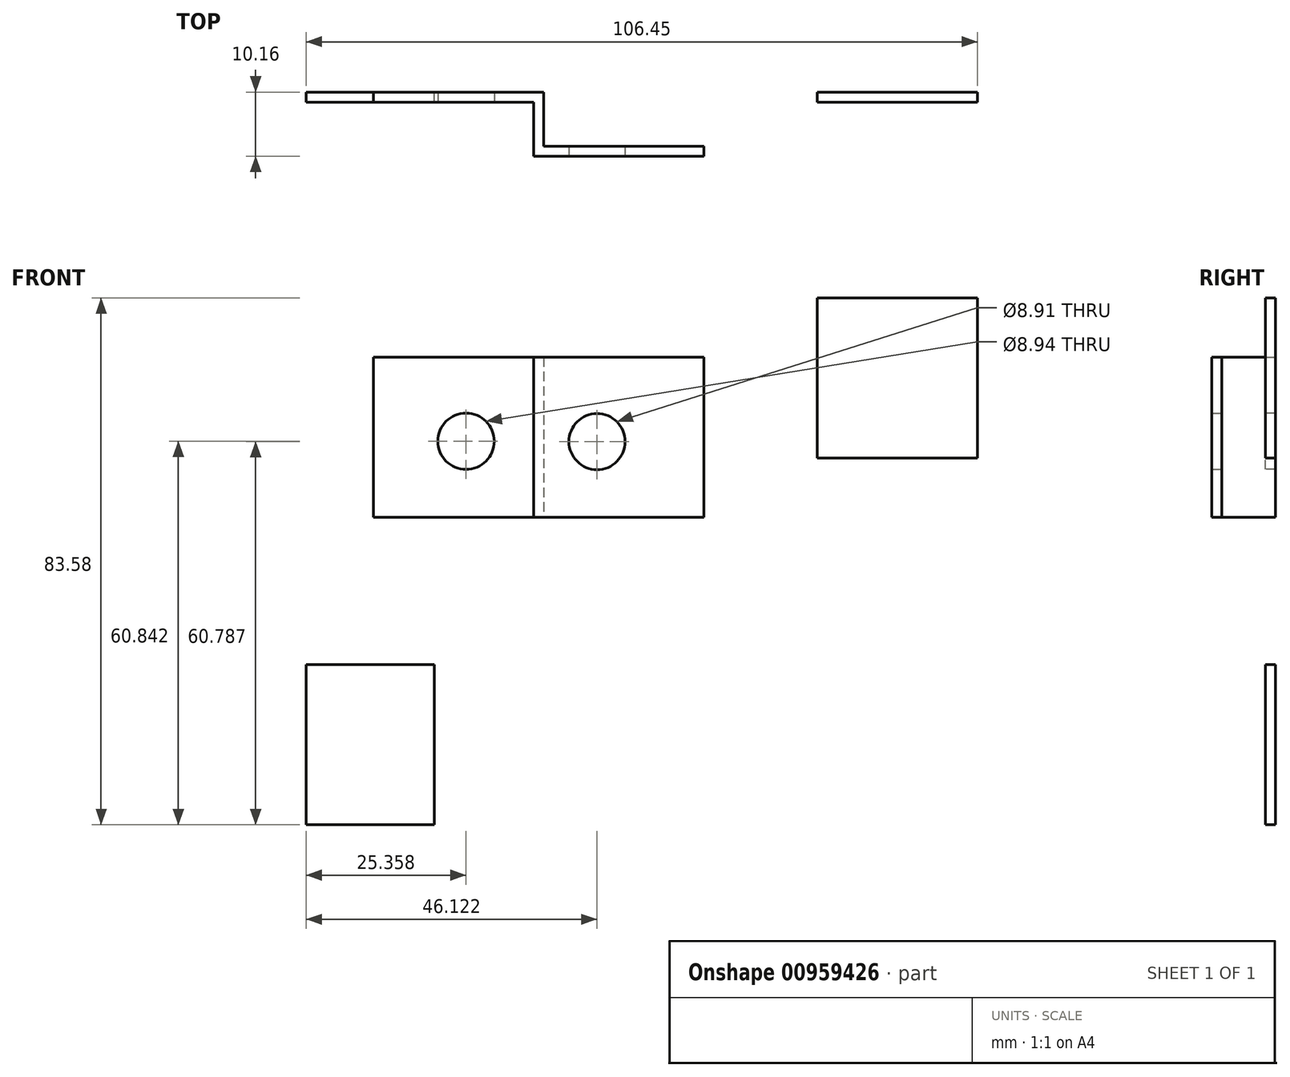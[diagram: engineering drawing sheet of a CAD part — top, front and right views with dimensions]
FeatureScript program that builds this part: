
annotation { "Feature Type Name" : "Feature", "Feature Type Description" : "" }
export const myFeature = defineFeature(function(context is Context, id is Id, definition is map)
    precondition{}
    {
        {
            var Q0;
            Q0=qCreatedBy(makeId("Front.planeOp"),FACE);
            var sketch = newSketch(context, id + "F0", { "sketchPlane" : qUnion([Q0])});
            skLineSegment(sketch, "E0.bottom", {"start": v(-49.08, 20.57) * mm, "end": v(-23.68, 20.57) * mm});
            skLineSegment(sketch, "E0.top", {"start": v(-49.08, -4.83) * mm, "end": v(-23.68, -4.83) * mm});
            skLineSegment(sketch, "E0.left", {"start": v(-49.08, 20.57) * mm, "end": v(-49.08, -4.83) * mm});
            skLineSegment(sketch, "E0.right", {"start": v(-23.68, 20.57) * mm, "end": v(-23.68, -4.83) * mm});
            skLineSegment(sketch, "E1.bottom", {"start": v(21.3, 29.98) * mm, "end": v(46.7, 29.98) * mm});
            skLineSegment(sketch, "E1.top", {"start": v(21.3, 4.57) * mm, "end": v(46.7, 4.57) * mm});
            skLineSegment(sketch, "E1.left", {"start": v(21.3, 29.98) * mm, "end": v(21.3, 4.57) * mm});
            skLineSegment(sketch, "E1.right", {"start": v(46.7, 29.98) * mm, "end": v(46.7, 4.57) * mm});
            skLineSegment(sketch, "E2.bottom", {"start": v(-23.68, 20.57) * mm, "end": v(-22.1, 20.57) * mm});
            skLineSegment(sketch, "E2.top", {"start": v(-23.68, -4.83) * mm, "end": v(-22.1, -4.83) * mm});
            skLineSegment(sketch, "E2.right", {"start": v(-22.1, 20.57) * mm, "end": v(-22.1, -4.83) * mm});
            skSolve(sketch);
        }
        {
            var Q0;
            Q0=makeQuery(id+"F0.imprint","IMPRINT",FACE,{"disambiguationData":[TD([[makeQuery(id+"F0.imprint","IMPRINT",EDGE,{"derivedFrom":sQuery(id+"F0.wireOp",EDGE,"E2.bottom")}),-1.0]])]});
            extrude(context, id + "F1", {"entities" : qUnion([Q0]), "depth" : 10.16 * mm, "offsetDistance" : 25.4 * mm});
        }
        {
            var Q0;
            Q0 = qSketchRegion(id + "F0", true);
            extrude(context, id + "F2", {"entities" : qUnion([Q0]), "operationType" : NewBodyOperationType.ADD, "depth" : 1.59 * mm, "offsetDistance" : 25.4 * mm});
        }
        {
            var Q0;
            Q0=makeQuery(id+"F1.opExtrude","CAP_FACE",FACE,{"disambiguationData":[OSD([sQuery(id+"F0.wireOp",EDGE,"E2.bottom"),sQuery(id+"F0.wireOp",EDGE,"E2.top"),sQuery(id+"F0.wireOp",EDGE,"E0.right"),sQuery(id+"F0.wireOp",EDGE,"E2.right")])],"isStart":false});
            var sketch = newSketch(context, id + "F3", { "sketchPlane" : qUnion([Q0])});
            skLineSegment(sketch, "E3.bottom", {"start": v(-22.1, 20.57) * mm, "end": v(3.32, 20.57) * mm});
            skLineSegment(sketch, "E3.top", {"start": v(-22.1, -4.83) * mm, "end": v(3.32, -4.83) * mm});
            skLineSegment(sketch, "E3.left", {"start": v(-22.1, 20.57) * mm, "end": v(-22.1, -4.83) * mm});
            skLineSegment(sketch, "E3.right", {"start": v(3.32, 20.57) * mm, "end": v(3.32, -4.83) * mm});
            skSolve(sketch);
        }
        {
            var Q0;
            Q0=makeQuery(id+"F3.imprint","IMPRINT",FACE,{"disambiguationData":[TD([[makeQuery(id+"F3.imprint","IMPRINT",EDGE,{"derivedFrom":sQuery(id+"F3.wireOp",EDGE,"E3.bottom")}),-1.0]])]});
            extrude(context, id + "F4", {"entities" : qUnion([Q0]), "operationType" : NewBodyOperationType.ADD, "depth" : -1.59 * mm, "offsetDistance" : 25.4 * mm});
        }
        {
            var Q0;
            Q0=qCreatedBy(makeId("Front.planeOp"),FACE);
            var sketch = newSketch(context, id + "F5", { "sketchPlane" : qUnion([Q0])});
            skLineSegment(sketch, "E4.bottom", {"start": v(-59.75, -28.2) * mm, "end": v(-39.42, -28.2) * mm});
            skLineSegment(sketch, "E4.top", {"start": v(-59.75, -53.6) * mm, "end": v(-39.42, -53.6) * mm});
            skLineSegment(sketch, "E4.left", {"start": v(-59.75, -28.2) * mm, "end": v(-59.75, -53.6) * mm});
            skLineSegment(sketch, "E4.right", {"start": v(-39.42, -28.2) * mm, "end": v(-39.42, -53.6) * mm});
            skSolve(sketch);
        }
        {
            var Q0;
            Q0=makeQuery(id+"F5.imprint","IMPRINT",FACE,{"disambiguationData":[TD([[makeQuery(id+"F5.imprint","IMPRINT",EDGE,{"derivedFrom":sQuery(id+"F5.wireOp",EDGE,"E4.bottom")}),-1.0]])]});
            extrude(context, id + "F6", {"entities" : qUnion([Q0]), "depth" : 1.59 * mm, "offsetDistance" : 25.4 * mm});
        }
        {
            var Q0;
            Q0=makeQuery(id+"F4.boolean.opBoolean","MERGE",FACE,{"derivedFrom":[makeQuery(id+"F1.opExtrude","CAP_FACE",FACE,{"disambiguationData":[OSD([sQuery(id+"F0.wireOp",EDGE,"E2.bottom"),sQuery(id+"F0.wireOp",EDGE,"E2.top"),sQuery(id+"F0.wireOp",EDGE,"E0.right"),sQuery(id+"F0.wireOp",EDGE,"E2.right")])],"isStart":false}),makeQuery(id+"F4.opExtrude","CAP_FACE",FACE,{"disambiguationData":[OSD([sQuery(id+"F3.wireOp",EDGE,"E3.bottom"),sQuery(id+"F3.wireOp",EDGE,"E3.top"),sQuery(id+"F3.wireOp",EDGE,"E3.left"),sQuery(id+"F3.wireOp",EDGE,"E3.right")])],"isStart":true})]});
            var sketch = newSketch(context, id + "F7", { "sketchPlane" : qUnion([Q0])});
            skCircle(sketch, "E5", {"center": v(-13.63, 7.19) * mm, "radius": 4.46 * mm});
            skSolve(sketch);
        }
        {
            var Q0;
            Q0=makeQuery(id+"F7.imprint","IMPRINT",FACE,{"disambiguationData":[TD([[makeQuery(id+"F7.imprint","IMPRINT",EDGE,{"derivedFrom":sQuery(id+"F7.wireOp",EDGE,"E5")}),1.0]])]});
            extrude(context, id + "F8", {"entities" : qUnion([Q0]), "operationType" : NewBodyOperationType.REMOVE, "oppositeDirection" : true, "depth" : 25.4 * mm, "offsetDistance" : 25.4 * mm});
        }
        {
            var Q0;
            Q0=makeQuery(id+"F2.opExtrude","CAP_FACE",FACE,{"disambiguationData":[OSD([sQuery(id+"F0.wireOp",EDGE,"E0.bottom"),sQuery(id+"F0.wireOp",EDGE,"E0.top"),sQuery(id+"F0.wireOp",EDGE,"E0.left"),sQuery(id+"F0.wireOp",EDGE,"E2.bottom"),sQuery(id+"F0.wireOp",EDGE,"E2.top"),sQuery(id+"F0.wireOp",EDGE,"E2.right")])],"isStart":false});
            var sketch = newSketch(context, id + "F9", { "sketchPlane" : qUnion([Q0])});
            skCircle(sketch, "E6", {"center": v(-34.4, 7.24) * mm, "radius": 4.47 * mm});
            skSolve(sketch);
        }
        {
            var Q0;
            Q0=makeQuery(id+"F9.imprint","IMPRINT",FACE,{"disambiguationData":[TD([[makeQuery(id+"F9.imprint","IMPRINT",EDGE,{"derivedFrom":sQuery(id+"F9.wireOp",EDGE,"E6")}),1.0]])]});
            extrude(context, id + "F10", {"entities" : qUnion([Q0]), "operationType" : NewBodyOperationType.REMOVE, "oppositeDirection" : true, "depth" : 25.4 * mm, "offsetDistance" : 25.4 * mm});
        }
    });
